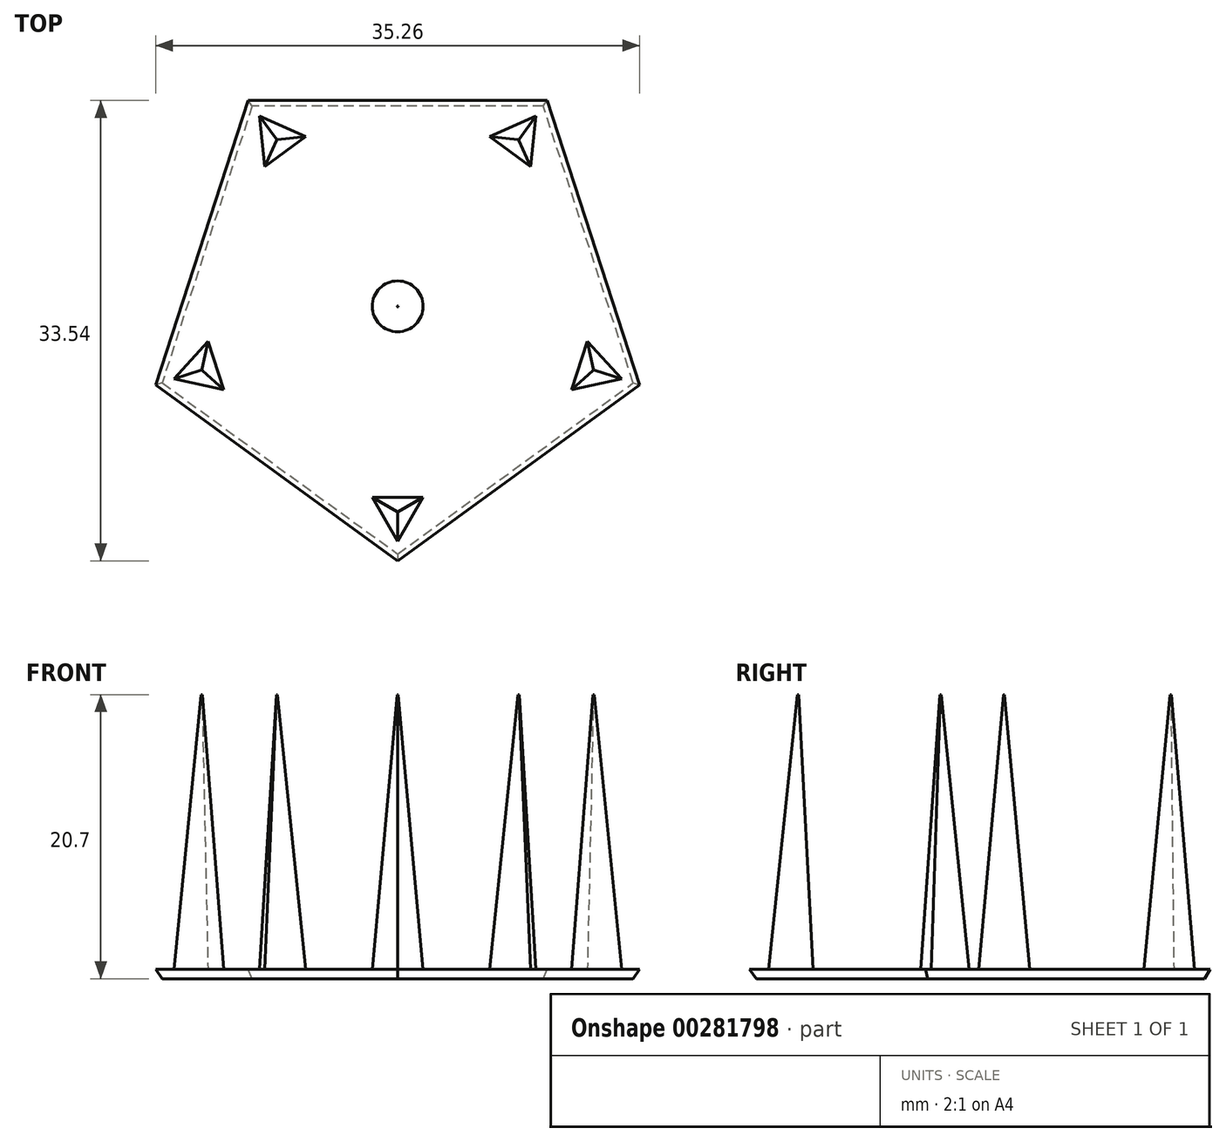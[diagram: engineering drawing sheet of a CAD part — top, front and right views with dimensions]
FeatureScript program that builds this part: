
annotation { "Feature Type Name" : "Feature", "Feature Type Description" : "" }
export const myFeature = defineFeature(function(context is Context, id is Id, definition is map)
    precondition{}
    {
        {
            var Q0;
            Q0=qCreatedBy(makeId("Top.planeOp"),FACE);
            var sketch = newSketch(context, id + "F0", { "sketchPlane" : qUnion([Q0])});
            skCircle(sketch, "E0.cCircle", {"center": v(0, 0) * mm, "radius": 15 * mm, "construction": true});
            skLineSegment(sketch, "E0.0", {"start": v(-10.9, 15) * mm, "end": v(10.9, 15) * mm});
            skLineSegment(sketch, "E0.1", {"start": v(10.9, 15) * mm, "end": v(17.63, -5.73) * mm});
            skLineSegment(sketch, "E0.2", {"start": v(17.63, -5.73) * mm, "end": v(0, -18.54) * mm});
            skLineSegment(sketch, "E0.3", {"start": v(0, -18.54) * mm, "end": v(-17.63, -5.73) * mm});
            skLineSegment(sketch, "E0.4", {"start": v(-17.63, -5.73) * mm, "end": v(-10.9, 15) * mm});
            skPoint(sketch, "E0.0.midPoint", {"position": v(0, 15) * mm});
            skCircle(sketch, "E1.cCircle", {"center": v(0, -15) * mm, "radius": 1.07 * mm, "construction": true});
            skLineSegment(sketch, "E1.0", {"start": v(-1.85, -13.93) * mm, "end": v(1.85, -13.93) * mm});
            skLineSegment(sketch, "E1.1", {"start": v(1.85, -13.93) * mm, "end": v(0, -17.14) * mm});
            skLineSegment(sketch, "E1.2", {"start": v(0, -17.14) * mm, "end": v(-1.85, -13.93) * mm});
            skPoint(sketch, "E1.0.midPoint", {"position": v(0, -13.93) * mm});
            skPoint(sketch, "E2.1.0", {"position": v(13.25, -4.3) * mm});
            skLineSegment(sketch, "E2.1.1", {"start": v(13.82, -2.54) * mm, "end": v(16.3, -5.3) * mm});
            skLineSegment(sketch, "E2.1.2", {"start": v(16.3, -5.3) * mm, "end": v(12.67, -6.07) * mm});
            skLineSegment(sketch, "E2.1.3", {"start": v(12.67, -6.07) * mm, "end": v(13.82, -2.54) * mm});
            skCircle(sketch, "E2.1.4", {"center": v(14.27, -4.64) * mm, "radius": 1.07 * mm, "construction": true});
            skPoint(sketch, "E2.2.0", {"position": v(8.19, 11.27) * mm});
            skLineSegment(sketch, "E2.2.1", {"start": v(6.69, 12.36) * mm, "end": v(10.08, 13.87) * mm});
            skLineSegment(sketch, "E2.2.2", {"start": v(10.08, 13.87) * mm, "end": v(9.69, 10.18) * mm});
            skLineSegment(sketch, "E2.2.3", {"start": v(9.69, 10.18) * mm, "end": v(6.69, 12.36) * mm});
            skCircle(sketch, "E2.2.4", {"center": v(8.82, 12.14) * mm, "radius": 1.07 * mm, "construction": true});
            skPoint(sketch, "E2.3.0", {"position": v(-8.19, 11.27) * mm});
            skLineSegment(sketch, "E2.3.1", {"start": v(-9.69, 10.18) * mm, "end": v(-10.08, 13.87) * mm});
            skLineSegment(sketch, "E2.3.2", {"start": v(-10.08, 13.87) * mm, "end": v(-6.69, 12.36) * mm});
            skLineSegment(sketch, "E2.3.3", {"start": v(-6.69, 12.36) * mm, "end": v(-9.69, 10.18) * mm});
            skCircle(sketch, "E2.3.4", {"center": v(-8.82, 12.14) * mm, "radius": 1.07 * mm, "construction": true});
            skPoint(sketch, "E2.4.0", {"position": v(-13.25, -4.3) * mm});
            skLineSegment(sketch, "E2.4.1", {"start": v(-12.67, -6.07) * mm, "end": v(-16.3, -5.3) * mm});
            skLineSegment(sketch, "E2.4.2", {"start": v(-16.3, -5.3) * mm, "end": v(-13.82, -2.54) * mm});
            skLineSegment(sketch, "E2.4.3", {"start": v(-13.82, -2.54) * mm, "end": v(-12.67, -6.07) * mm});
            skCircle(sketch, "E2.4.4", {"center": v(-14.27, -4.64) * mm, "radius": 1.07 * mm, "construction": true});
            skCircle(sketch, "E3", {"center": v(0, 0) * mm, "radius": 1.85 * mm});
            skLineSegment(sketch, "E4", {"start": v(0, -1.85) * mm, "end": v(0, 1.85) * mm, "construction": true});
            skSolve(sketch);
        }
        {
            var Q0;
            Q0 = qSketchRegion(id + "F0", true);
            var Q1;
            Q1=makeQuery(id+"F0.imprint","IMPRINT",FACE,{"disambiguationData":[TD([[makeQuery(id+"F0.imprint","IMPRINT",EDGE,{"derivedFrom":sQuery(id+"F0.wireOp",EDGE,"E2.1.1")}),-1.0]])]});
            var Q2;
            Q2=makeQuery(id+"F0.imprint","IMPRINT",FACE,{"disambiguationData":[TD([[makeQuery(id+"F0.imprint","IMPRINT",EDGE,{"derivedFrom":sQuery(id+"F0.wireOp",EDGE,"E2.2.1")}),-1.0]])]});
            var Q3;
            Q3=makeQuery(id+"F0.imprint","IMPRINT",FACE,{"disambiguationData":[TD([[makeQuery(id+"F0.imprint","IMPRINT",EDGE,{"derivedFrom":sQuery(id+"F0.wireOp",EDGE,"E2.3.1")}),-1.0]])]});
            var Q4;
            Q4=makeQuery(id+"F0.imprint","IMPRINT",FACE,{"disambiguationData":[TD([[makeQuery(id+"F0.imprint","IMPRINT",EDGE,{"derivedFrom":sQuery(id+"F0.wireOp",EDGE,"71d2bd87-af98-46aa-9332-39a8f33fdb51.0")}),-1.0]])]});
            var Q5;
            Q5=makeQuery(id+"F0.imprint","IMPRINT",FACE,{"disambiguationData":[TD([[makeQuery(id+"F0.imprint","IMPRINT",EDGE,{"derivedFrom":sQuery(id+"F0.wireOp",EDGE,"E1.0")}),-1.0]])]});
            var Q6;
            Q6=makeQuery(id+"F0.imprint","IMPRINT",FACE,{"disambiguationData":[TD([[makeQuery(id+"F0.imprint","IMPRINT",EDGE,{"derivedFrom":sQuery(id+"F0.wireOp",EDGE,"E2.4.1")}),-1.0]])]});
            var Q7;
            Q7=makeQuery(id+"F0.imprint","IMPRINT",FACE,{"disambiguationData":[TD([[makeQuery(id+"F0.imprint","IMPRINT",EDGE,{"derivedFrom":sQuery(id+"F0.wireOp",EDGE,"E3")}),1.0]])]});
            extrude(context, id + "F1", {"entities" : qUnion([Q0, Q1, Q2, Q3, Q4, Q5, Q6, Q7]), "oppositeDirection" : true, "depth" : 0.7 * mm, "hasDraft" : true, "draftAngle" : 30 * degree, "draftPullDirection" : true});
        }
        {
            var Q0;
            Q0=makeQuery(id+"F0.imprint","IMPRINT",FACE,{"disambiguationData":[TD([[makeQuery(id+"F0.imprint","IMPRINT",EDGE,{"derivedFrom":sQuery(id+"F0.wireOp",EDGE,"E2.2.1")}),-1.0]])]});
            var Q1;
            Q1=makeQuery(id+"F0.imprint","IMPRINT",FACE,{"disambiguationData":[TD([[makeQuery(id+"F0.imprint","IMPRINT",EDGE,{"derivedFrom":sQuery(id+"F0.wireOp",EDGE,"E2.1.1")}),-1.0]])]});
            var Q2;
            Q2=makeQuery(id+"F0.imprint","IMPRINT",FACE,{"disambiguationData":[TD([[makeQuery(id+"F0.imprint","IMPRINT",EDGE,{"derivedFrom":sQuery(id+"F0.wireOp",EDGE,"71d2bd87-af98-46aa-9332-39a8f33fdb51.0")}),-1.0]])]});
            var Q3;
            Q3=makeQuery(id+"F0.imprint","IMPRINT",FACE,{"disambiguationData":[TD([[makeQuery(id+"F0.imprint","IMPRINT",EDGE,{"derivedFrom":sQuery(id+"F0.wireOp",EDGE,"E2.3.1")}),-1.0]])]});
            var Q4;
            Q4=makeQuery(id+"F0.imprint","IMPRINT",FACE,{"disambiguationData":[TD([[makeQuery(id+"F0.imprint","IMPRINT",EDGE,{"derivedFrom":sQuery(id+"F0.wireOp",EDGE,"E2.4.1")}),-1.0]])]});
            var Q5;
            Q5=makeQuery(id+"F0.imprint","IMPRINT",FACE,{"disambiguationData":[TD([[makeQuery(id+"F0.imprint","IMPRINT",EDGE,{"derivedFrom":sQuery(id+"F0.wireOp",EDGE,"E1.0")}),-1.0]])]});
            extrude(context, id + "F2", {"entities" : qUnion([Q0, Q1, Q2, Q3, Q4, Q5]), "operationType" : NewBodyOperationType.ADD, "depth" : 20 * mm, "hasDraft" : true, "draftAngle" : 3 * degree, "draftPullDirection" : true});
        }
        {
            var Q0;
            Q0=makeQuery(id+"F0.imprint","IMPRINT",FACE,{"disambiguationData":[TD([[makeQuery(id+"F0.imprint","IMPRINT",EDGE,{"derivedFrom":sQuery(id+"F0.wireOp",EDGE,"E3")}),1.0]])]});
            extrude(context, id + "F3", {"entities" : qUnion([Q0]), "operationType" : NewBodyOperationType.ADD, "depth" : 20 * mm, "hasDraft" : true, "draftAngle" : 5.2 * degree, "draftPullDirection" : true});
        }
    });
